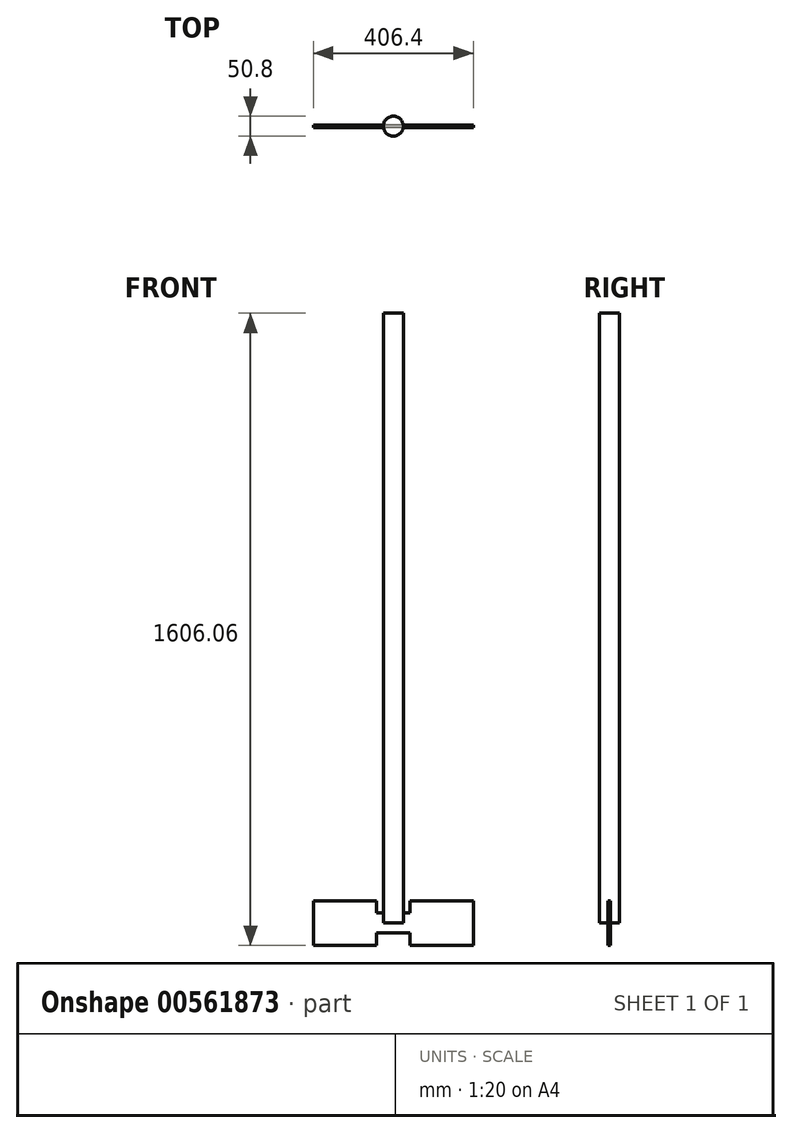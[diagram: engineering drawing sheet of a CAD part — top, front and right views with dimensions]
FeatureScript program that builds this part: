
annotation { "Feature Type Name" : "Feature", "Feature Type Description" : "" }
export const myFeature = defineFeature(function(context is Context, id is Id, definition is map)
    precondition{}
    {
        {
            var Q0;
            Q0=qCreatedBy(makeId("Front.planeOp"),FACE);
            var sketch = newSketch(context, id + "F0", { "sketchPlane" : qUnion([Q0])});
            skLineSegment(sketch, "E0.bottom", {"start": v(42.88, 25.4) * mm, "end": v(-42.88, 25.4) * mm});
            skLineSegment(sketch, "E0.top", {"start": v(42.88, -25.4) * mm, "end": v(-42.88, -25.4) * mm});
            skLineSegment(sketch, "E0.left", {"start": v(42.88, 25.4) * mm, "end": v(42.88, -25.4) * mm});
            skLineSegment(sketch, "E0.right", {"start": v(-42.88, 25.4) * mm, "end": v(-42.88, -25.4) * mm});
            skPoint(sketch, "E0.middle", {"position": v(0, 0) * mm});
            skLineSegment(sketch, "E1.bottom", {"start": v(-42.88, 56.66) * mm, "end": v(-203.2, 56.66) * mm});
            skLineSegment(sketch, "E1.top", {"start": v(-42.88, -56.66) * mm, "end": v(-203.2, -56.66) * mm});
            skLineSegment(sketch, "E1.left", {"start": v(-42.88, 56.66) * mm, "end": v(-42.88, -56.66) * mm});
            skLineSegment(sketch, "E1.right", {"start": v(-203.2, 56.66) * mm, "end": v(-203.2, -56.66) * mm});
            skPoint(sketch, "E1.middle", {"position": v(-123.04, 0) * mm});
            skLineSegment(sketch, "E2.MirrorCS", {"start": v(42.88, 56.66) * mm, "end": v(203.2, 56.66) * mm});
            skPoint(sketch, "E3.MirrorP", {"position": v(123.04, 0) * mm});
            skLineSegment(sketch, "E4.MirrorCS", {"start": v(42.88, -56.66) * mm, "end": v(203.2, -56.66) * mm});
            skLineSegment(sketch, "E5.MirrorCS", {"start": v(203.2, 56.66) * mm, "end": v(203.2, -56.66) * mm});
            skLineSegment(sketch, "E6.MirrorCS", {"start": v(42.88, 56.66) * mm, "end": v(42.88, -56.66) * mm});
            skSolve(sketch);
        }
        {
            var Q0;
            Q0=qCreatedBy(makeId("Top.planeOp"),FACE);
            var sketch = newSketch(context, id + "F1", { "sketchPlane" : qUnion([Q0])});
            skCircle(sketch, "E7", {"center": v(0, 0) * mm, "radius": 25.4 * mm});
            skSolve(sketch);
        }
        {
            var Q0;
            Q0 = qSketchRegion(id + "F0", true);
            extrude(context, id + "F2", {"entities" : qUnion([Q0]), "endBound" : BoundingType.SYMMETRIC, "depth" : 6.35 * mm, "offsetDistance" : 25.4 * mm});
        }
        {
            var Q0;
            Q0=sQuery(id+"F1.wireOp",EDGE,"E7");
            extrude(context, id + "F3", {"bodyType" : ToolBodyType.SURFACE, "surfaceEntities" : qUnion([Q0]), "oppositeDirection" : true, "depth" : 25.4 * mm, "offsetDistance" : 25.4 * mm});
        }
        {
            var Q0;
            Q0 = qSketchRegion(id + "F1", true);
            extrude(context, id + "F4", {"entities" : qUnion([Q0]), "operationType" : NewBodyOperationType.ADD, "depth" : 1549.4 * mm, "offsetDistance" : 25.4 * mm});
        }
    });
